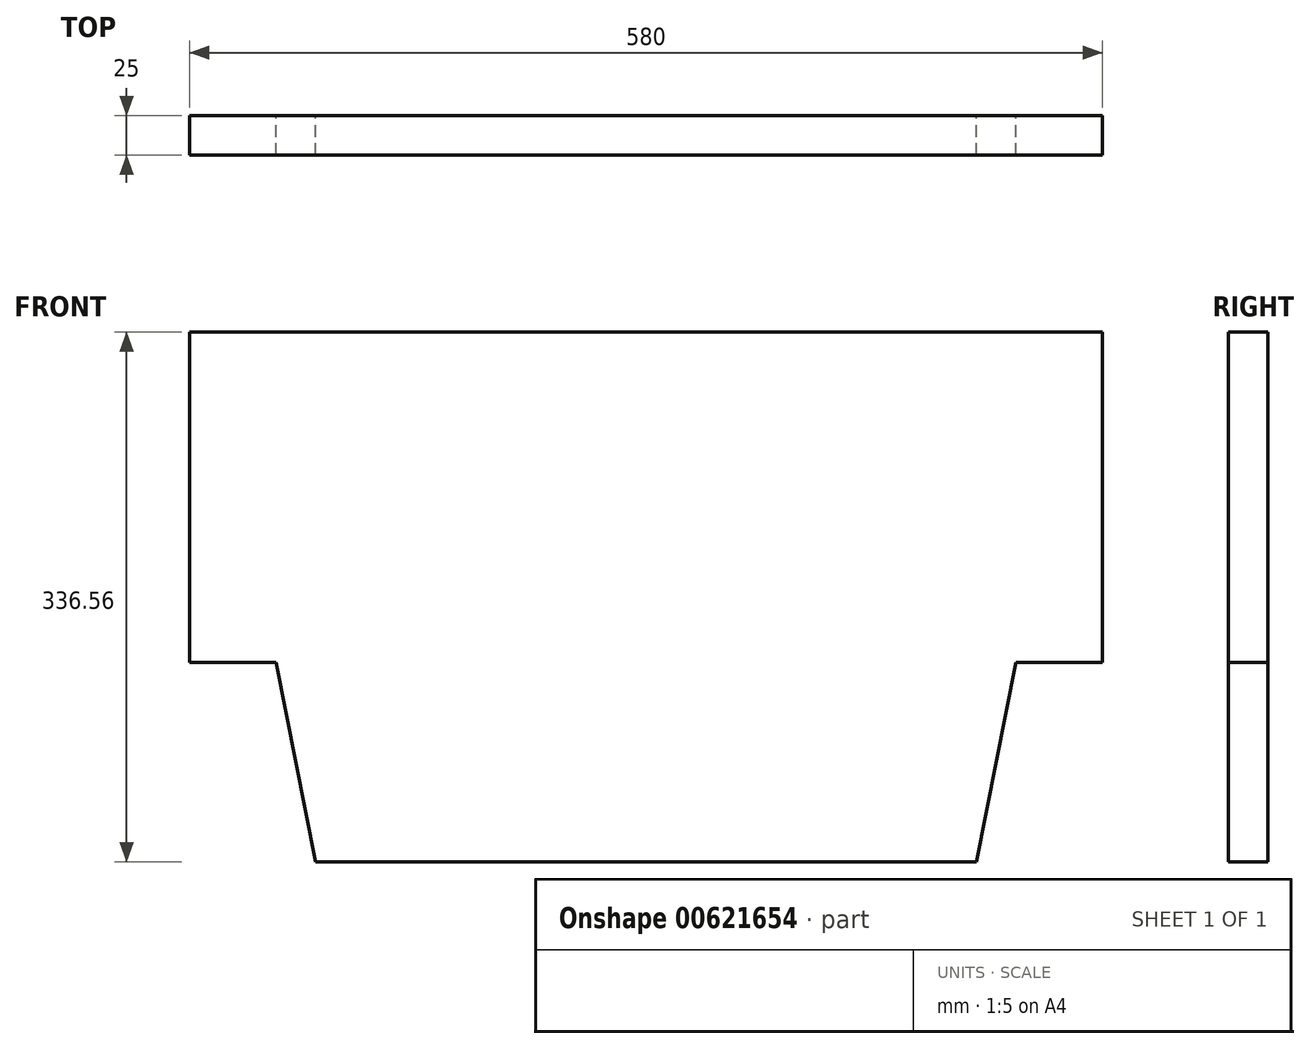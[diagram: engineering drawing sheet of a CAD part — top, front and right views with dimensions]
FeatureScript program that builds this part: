
annotation { "Feature Type Name" : "Feature", "Feature Type Description" : "" }
export const myFeature = defineFeature(function(context is Context, id is Id, definition is map)
    precondition{}
    {
        {
            var Q0;
            Q0=qCreatedBy(makeId("Front.planeOp"),FACE);
            var sketch = newSketch(context, id + "F0", { "sketchPlane" : qUnion([Q0])});
            skLineSegment(sketch, "E0", {"start": v(0, 0) * mm, "end": v(-9.91, 50) * mm, "construction": true});
            skLineSegment(sketch, "E1", {"start": v(-35, 176.56) * mm, "end": v(-90, 176.56) * mm});
            skLineSegment(sketch, "E2", {"start": v(-90, 176.56) * mm, "end": v(-90, 386.56) * mm});
            skLineSegment(sketch, "E3", {"start": v(-90, 386.56) * mm, "end": v(490, 386.56) * mm});
            skLineSegment(sketch, "E4", {"start": v(490, 386.56) * mm, "end": v(490, 176.56) * mm});
            skLineSegment(sketch, "E5", {"start": v(490, 176.56) * mm, "end": v(435, 176.56) * mm});
            skLineSegment(sketch, "E6", {"start": v(435, 176.56) * mm, "end": v(409.91, 50) * mm});
            skLineSegment(sketch, "E7", {"start": v(400, 0) * mm, "end": v(0, 0) * mm, "construction": true});
            skLineSegment(sketch, "E8", {"start": v(200, 0) * mm, "end": v(200, 386.56) * mm, "construction": true});
            skLineSegment(sketch, "E9", {"start": v(409.91, 50) * mm, "end": v(409.91, 50) * mm});
            skLineSegment(sketch, "E10", {"start": v(-9.91, 50) * mm, "end": v(-9.91, 50) * mm});
            skLineSegment(sketch, "E11", {"start": v(409.91, 50) * mm, "end": v(-9.91, 50) * mm});
            skLineSegment(sketch, "E12", {"start": v(409.91, 50) * mm, "end": v(400, 0) * mm, "construction": true});
            skLineSegment(sketch, "E13", {"start": v(-9.91, 50) * mm, "end": v(-35, 176.56) * mm});
            skSolve(sketch);
        }
        {
            var Q0;
            Q0 = qSketchRegion(id + "F0", true);
            extrude(context, id + "F1", {"entities" : qUnion([Q0]), "depth" : 25 * mm, "offsetDistance" : 25 * mm});
        }
    });
